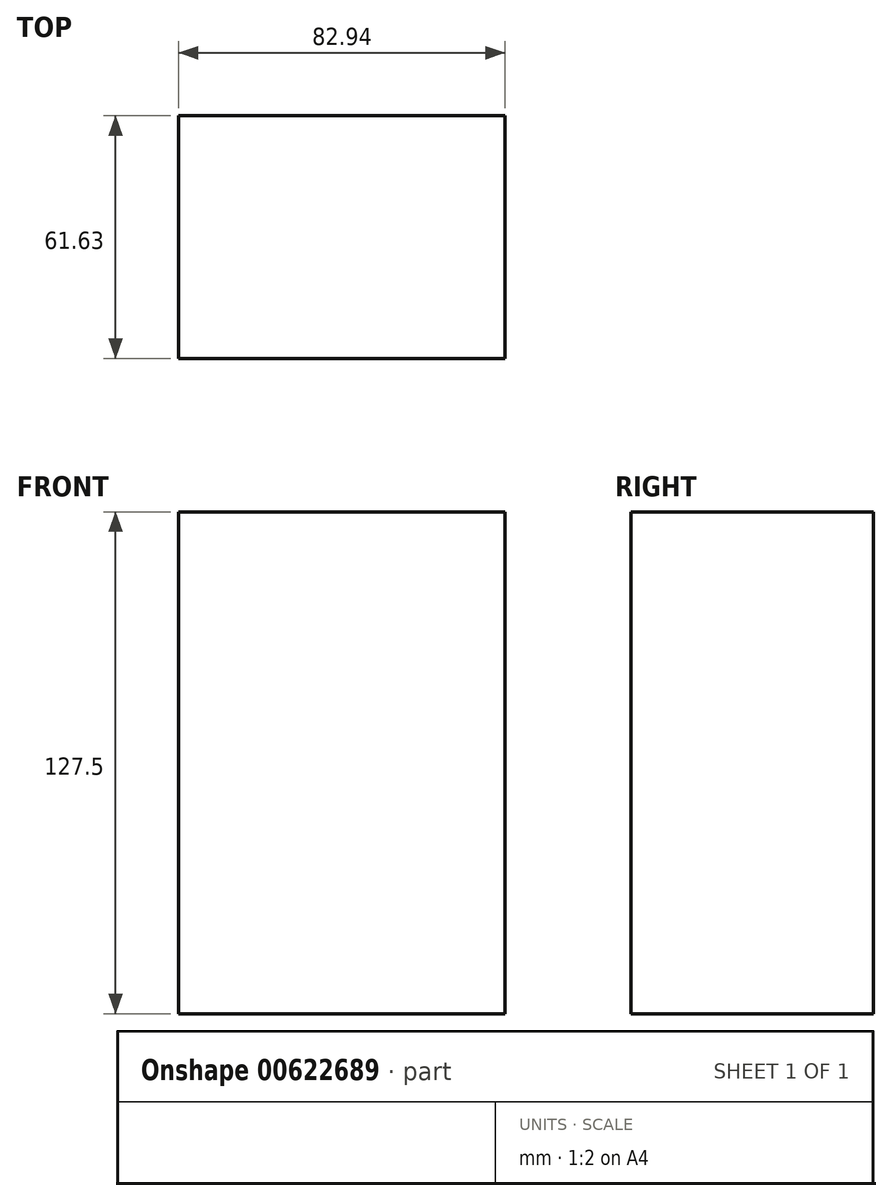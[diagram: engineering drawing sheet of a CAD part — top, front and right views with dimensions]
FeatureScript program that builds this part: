
annotation { "Feature Type Name" : "Feature", "Feature Type Description" : "" }
export const myFeature = defineFeature(function(context is Context, id is Id, definition is map)
    precondition{}
    {
        {
            var Q0;
            Q0=qCreatedBy(makeId("Top.planeOp"),FACE);
            var sketch = newSketch(context, id + "F0", { "sketchPlane" : qUnion([Q0])});
            skLineSegment(sketch, "E0.bottom", {"start": v(-41.38, 29.13) * mm, "end": v(41.56, 29.13) * mm});
            skLineSegment(sketch, "E0.top", {"start": v(-41.38, -32.5) * mm, "end": v(41.56, -32.5) * mm});
            skLineSegment(sketch, "E0.left", {"start": v(-41.38, 29.13) * mm, "end": v(-41.38, -32.5) * mm});
            skLineSegment(sketch, "E0.right", {"start": v(41.56, 29.13) * mm, "end": v(41.56, -32.5) * mm});
            skSolve(sketch);
        }
        {
            var Q0;
            Q0 = qSketchRegion(id + "F0", true);
            extrude(context, id + "F1", {"entities" : qUnion([Q0]), "depth" : 127.5 * mm, "offsetDistance" : 25 * mm});
        }
    });
